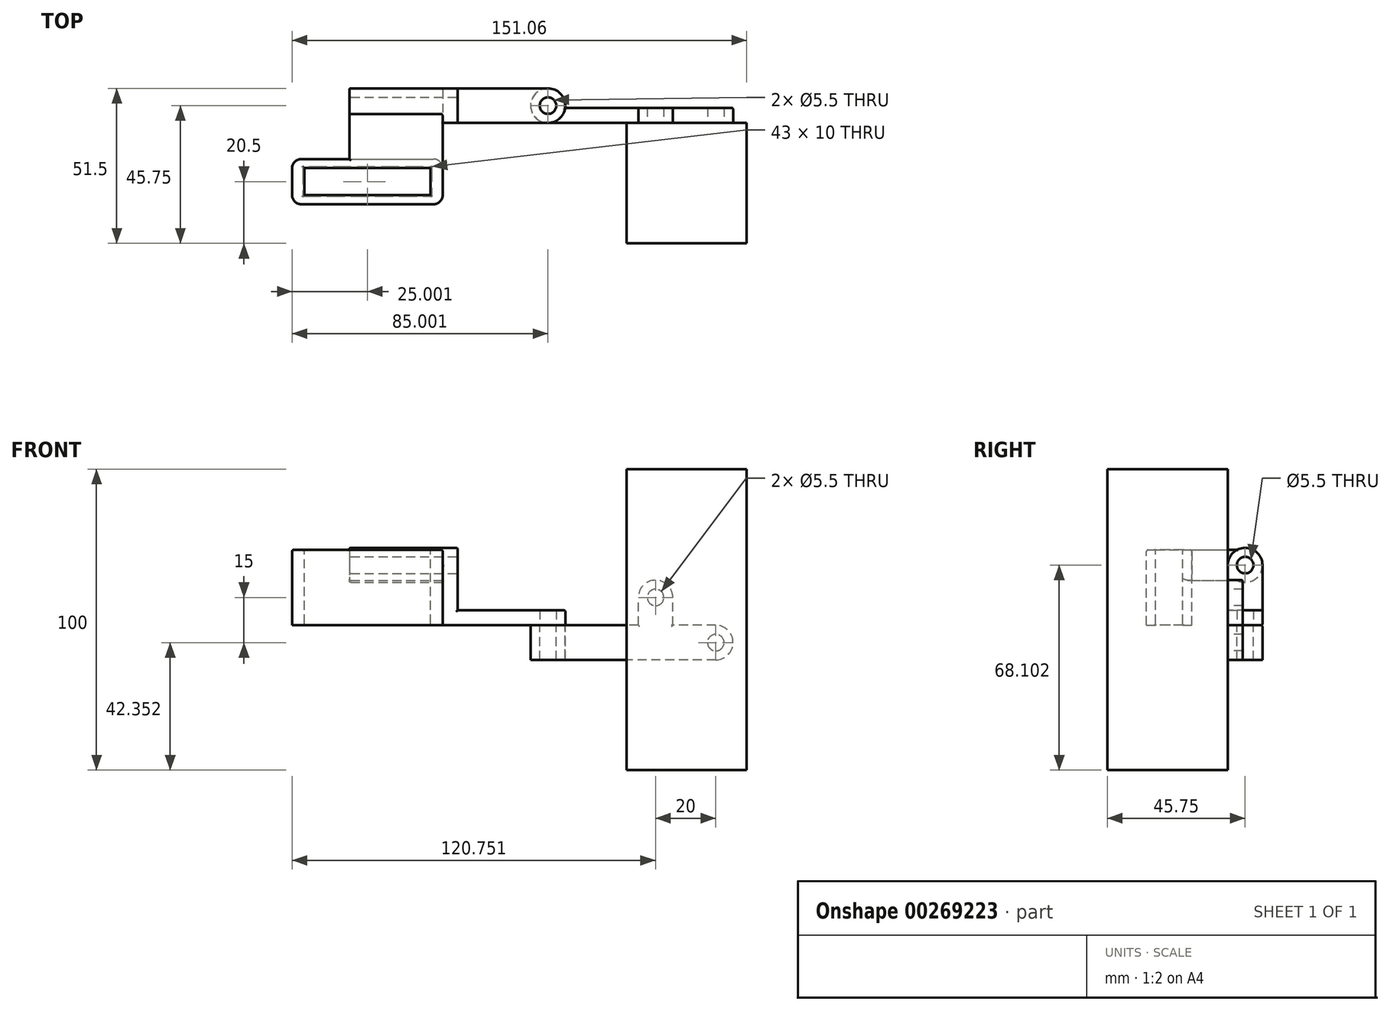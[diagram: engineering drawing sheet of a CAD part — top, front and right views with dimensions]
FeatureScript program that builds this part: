
annotation { "Feature Type Name" : "Feature", "Feature Type Description" : "" }
export const myFeature = defineFeature(function(context is Context, id is Id, definition is map)
    precondition{}
    {
        {
            var Q0;
            Q0=qCreatedBy(makeId("Top.planeOp"),FACE);
            var sketch = newSketch(context, id + "F0", { "sketchPlane" : qUnion([Q0])});
            skLineSegment(sketch, "E0.bottom", {"start": v(-20, 20) * mm, "end": v(20, 20) * mm});
            skLineSegment(sketch, "E0.top", {"start": v(-20, -20) * mm, "end": v(20, -20) * mm});
            skLineSegment(sketch, "E0.left", {"start": v(-20, 20) * mm, "end": v(-20, -20) * mm});
            skLineSegment(sketch, "E0.right", {"start": v(20, 20) * mm, "end": v(20, -20) * mm});
            skPoint(sketch, "E0.middle", {"position": v(0, 0) * mm});
            skSolve(sketch);
        }
        {
            var Q0;
            Q0=makeQuery(id+"F0.imprint","IMPRINT",FACE,{"disambiguationData":[TD([[makeQuery(id+"F0.imprint","IMPRINT",EDGE,{"derivedFrom":sQuery(id+"F0.wireOp",EDGE,"E0.bottom")}),-1.0]])]});
            extrude(context, id + "F1", {"entities" : qUnion([Q0]), "depth" : 100 * mm});
        }
        {
            var Q0;
            Q0=makeQuery(id+"F1.opExtrude","SWEPT_FACE",FACE,{"disambiguationData":[OSD([sQuery(id+"F0.wireOp",EDGE,"E0.bottom")])]});
            var sketch = newSketch(context, id + "F2", { "sketchPlane" : qUnion([Q0])});
            skPoint(sketch, "E1", {"position": v(-9.7, 42.35) * mm});
            skPoint(sketch, "E2", {"position": v(10.3, 57.35) * mm});
            skCircle(sketch, "E3", {"center": v(-9.7, 42.35) * mm, "radius": 5.75 * mm});
            skCircle(sketch, "E4", {"center": v(10.3, 57.35) * mm, "radius": 5.75 * mm});
            skLineSegment(sketch, "E5", {"start": v(-9.7, 48.1) * mm, "end": v(4.56, 48.1) * mm});
            skLineSegment(sketch, "E6", {"start": v(4.56, 48.1) * mm, "end": v(4.56, 57.35) * mm});
            skLineSegment(sketch, "E7", {"start": v(-9.7, 36.6) * mm, "end": v(16.06, 36.6) * mm});
            skLineSegment(sketch, "E8", {"start": v(16.06, 36.6) * mm, "end": v(16.06, 57.35) * mm});
            skLineSegment(sketch, "E9", {"start": v(16.06, 48.1) * mm, "end": v(46.06, 48.1) * mm});
            skLineSegment(sketch, "E10", {"start": v(46.06, 48.1) * mm, "end": v(46.06, 36.6) * mm});
            skLineSegment(sketch, "E11", {"start": v(46.06, 36.6) * mm, "end": v(16.06, 36.6) * mm});
            skSolve(sketch);
        }
        {
            var Q0;
            {var subQ0=sQuery(id+"F2.wireOp",EDGE,"E3");var subQ1=makeQuery(id+"F2.imprint","INTERSECT",VERTEX,{"derivedFrom":[subQ0,sQuery(id+"F2.wireOp",EDGE,"E5")]});Q0=makeQuery(id+"F2.imprint","IMPRINT",FACE,{"disambiguationData":[TD([[makeQuery(id+"F2.imprint","IMPRINT",EDGE,{"disambiguationData":[TD([[subQ1,-1.0]])],"derivedFrom":subQ0}),1.0]])]});}
            var Q1;
            {var subQ0=sQuery(id+"F2.wireOp",EDGE,"E4");var subQ1=makeQuery(id+"F2.imprint","INTERSECT",VERTEX,{"derivedFrom":[subQ0,sQuery(id+"F2.wireOp",EDGE,"E6")]});Q1=makeQuery(id+"F2.imprint","IMPRINT",FACE,{"disambiguationData":[TD([[makeQuery(id+"F2.imprint","IMPRINT",EDGE,{"disambiguationData":[TD([[subQ1,1.0]])],"derivedFrom":subQ0}),1.0]])]});}
            var Q2;
            {var subQ1=sQuery(id+"F2.wireOp",EDGE,"E5");Q2=makeQuery(id+"F2.imprint","IMPRINT",FACE,{"disambiguationData":[TD([[makeQuery(id+"F2.imprint","IMPRINT",EDGE,{"derivedFrom":subQ1}),-1.0]])]});}
            var Q3;
            {var subQ0=sQuery(id+"F2.wireOp",EDGE,"E10");Q3=makeQuery(id+"F2.imprint","IMPRINT",FACE,{"disambiguationData":[TD([[makeQuery(id+"F2.imprint","IMPRINT",EDGE,{"derivedFrom":subQ0}),-1.0]])]});}
            var Q4;
            {var subQ1=sQuery(id+"F2.wireOp",EDGE,"E8");var subQ3=sQuery(id+"F2.wireOp",EDGE,"E9");var subQ4=makeQuery(id+"F2.imprint","INTERSECT",VERTEX,{"derivedFrom":[subQ1,subQ3]});Q4=makeQuery(id+"F2.imprint","IMPRINT",FACE,{"disambiguationData":[TD([[makeQuery(id+"F2.imprint","IMPRINT",EDGE,{"disambiguationData":[TD([[subQ4,1.0]])],"derivedFrom":subQ1}),-1.0]])]});}
            extrude(context, id + "F3", {"entities" : qUnion([Q0, Q1, Q2, Q3, Q4]), "depth" : 5 * mm});
        }
        {
            var Q0;
            Q0=sQuery(id+"F2.wireOp",VERTEX,"E2");
            var Q1;
            Q1=sQuery(id+"F2.wireOp",VERTEX,"E1");
            var Q2;
            Q2=makeQuery(id+"F3.opExtrude","SWEPT_BODY",BODY,{"disambiguationData":[OSD([sQuery(id+"F2.wireOp",EDGE,"E3"),sQuery(id+"F2.wireOp",EDGE,"E4"),sQuery(id+"F2.wireOp",EDGE,"E5"),sQuery(id+"F2.wireOp",EDGE,"E6"),sQuery(id+"F2.wireOp",EDGE,"E7"),sQuery(id+"F2.wireOp",EDGE,"E8"),sQuery(id+"F2.wireOp",EDGE,"E9"),sQuery(id+"F2.wireOp",EDGE,"E10"),sQuery(id+"F2.wireOp",EDGE,"E11")])]});
            hole(context, id + "F4", {"style" : HoleStyle.SIMPLE, "endStyle" : HoleEndStyle.THROUGH, "oppositeDirection" : true, "standardTappedOrClearance" : lookupTablePath({ "standard" : "ISO", "fit" : "Normal", "size" : "M5", "type" : "Clearance" }), "standardBlindInLast" : lookupTablePath({ "fit" : "Standard", "standard" : "ISO", "size" : "M5", "type" : "Clearance" }), "holeDiameter" : 5.5 * mm, "isTappedThrough" : true, "tappedDepth" : 13.2 * mm, "tapClearance" : 3, "startFromSketch" : true, "locations" : qUnion([Q0, Q1]), "scope" : qUnion([Q2])});
        }
        {
            var Q0;
            Q0=makeQuery(id+"F3.opExtrude","SWEPT_FACE",FACE,{"disambiguationData":[OSD([sQuery(id+"F2.wireOp",EDGE,"E9")])]});
            var sketch = newSketch(context, id + "F5", { "sketchPlane" : qUnion([Q0])});
            skPoint(sketch, "E12", {"position": v(-46.06, 25.75) * mm});
            skCircle(sketch, "E13", {"center": v(-46.06, 25.75) * mm, "radius": 5.75 * mm});
            skSolve(sketch);
        }
        {
            var Q0;
            {var subQ1=sQuery(id+"F2.wireOp",EDGE,"E9");var subQ2=makeQuery(id+"F3.opExtrude","SWEPT_EDGE",EDGE,{"disambiguationData":[OSD([subQ1,sQuery(id+"F2.wireOp",EDGE,"E10")])]});Q0=makeQuery(id+"F5.imprint","IMPRINT",FACE,{"disambiguationData":[TD([[makeQuery(id+"F5.imprint","IMPRINT",EDGE,{"derivedFrom":subQ2}),-1.0]])]});}
            var Q1;
            Q1=makeQuery(id+"F3.opExtrude","SWEPT_FACE",FACE,{"disambiguationData":[OSD([sQuery(id+"F2.wireOp",EDGE,"E7"),sQuery(id+"F2.wireOp",EDGE,"E11")])]});
            extrude(context, id + "F6", {"entities" : qUnion([Q0]), "operationType" : NewBodyOperationType.ADD, "endBound" : BoundingType.UP_TO_SURFACE, "oppositeDirection" : true, "endBoundEntityFace" : qUnion([Q1]), "depth" : 25 * mm});
        }
        {
            var Q0;
            Q0=sQuery(id+"F5.wireOp",VERTEX,"E12");
            var Q1;
            Q1=makeQuery(id+"F3.opExtrude","SWEPT_BODY",BODY,{"disambiguationData":[OSD([sQuery(id+"F2.wireOp",EDGE,"E3"),sQuery(id+"F2.wireOp",EDGE,"E4"),sQuery(id+"F2.wireOp",EDGE,"E5"),sQuery(id+"F2.wireOp",EDGE,"E6"),sQuery(id+"F2.wireOp",EDGE,"E7"),sQuery(id+"F2.wireOp",EDGE,"E8"),sQuery(id+"F2.wireOp",EDGE,"E9"),sQuery(id+"F2.wireOp",EDGE,"E10"),sQuery(id+"F2.wireOp",EDGE,"E11")])]});
            hole(context, id + "F7", {"style" : HoleStyle.SIMPLE, "endStyle" : HoleEndStyle.THROUGH, "standardTappedOrClearance" : lookupTablePath({ "standard" : "ISO", "fit" : "Normal", "size" : "M5", "type" : "Clearance" }), "standardBlindInLast" : lookupTablePath({ "fit" : "Standard", "standard" : "ISO", "size" : "M5", "type" : "Clearance" }), "holeDiameter" : 5.5 * mm, "isTappedThrough" : true, "tappedDepth" : 13.2 * mm, "tapClearance" : 3, "startFromSketch" : true, "locations" : qUnion([Q0]), "scope" : qUnion([Q1])});
        }
        {
            var Q0;
            {var subQ1=sQuery(id+"F2.wireOp",EDGE,"E9");var subQ2=makeQuery(id+"F3.opExtrude","CAP_EDGE",EDGE,{"disambiguationData":[OSD([subQ1])],"isStart":true});Q0=makeQuery(id+"F5.imprint","IMPRINT",FACE,{"disambiguationData":[TD([[makeQuery(id+"F5.imprint","IMPRINT",EDGE,{"derivedFrom":subQ2}),-1.0]])]});}
            var sketch = newSketch(context, id + "F8", { "sketchPlane" : qUnion([Q0])});
            skPoint(sketch, "E14", {"position": v(-46.06, 25.75) * mm});
            skCircle(sketch, "E15", {"center": v(-46.06, 25.75) * mm, "radius": 5.75 * mm});
            skLineSegment(sketch, "E16", {"start": v(-46.06, 31.5) * mm, "end": v(-76.06, 31.5) * mm});
            skLineSegment(sketch, "E17", {"start": v(-76.06, 31.5) * mm, "end": v(-76.06, 20) * mm});
            skLineSegment(sketch, "E18", {"start": v(-76.06, 20) * mm, "end": v(-46.06, 20) * mm});
            skSolve(sketch);
        }
        {
            var Q0;
            {var subQ2=sQuery(id+"F8.wireOp",EDGE,"E16");Q0=makeQuery(id+"F8.imprint","IMPRINT",FACE,{"disambiguationData":[TD([[makeQuery(id+"F8.imprint","IMPRINT",EDGE,{"derivedFrom":subQ2}),1.0]])]});}
            var Q1;
            {var subQ0=sQuery(id+"F8.wireOp",EDGE,"E15");var subQ3=makeQuery(id+"F8.imprint","INTERSECT",VERTEX,{"derivedFrom":[subQ0,sQuery(id+"F8.wireOp",EDGE,"E16")]});Q1=makeQuery(id+"F8.imprint","IMPRINT",FACE,{"disambiguationData":[TD([[makeQuery(id+"F8.imprint","IMPRINT",EDGE,{"disambiguationData":[TD([[subQ3,-1.0]])],"derivedFrom":subQ0}),1.0]])]});}
            extrude(context, id + "F9", {"entities" : qUnion([Q0, Q1]), "depth" : 5 * mm});
        }
        {
            var Q0;
            Q0=sQuery(id+"F5.wireOp",VERTEX,"E12");
            var Q1;
            Q1=makeQuery(id+"F9.opExtrude","SWEPT_BODY",BODY,{"disambiguationData":[OSD([sQuery(id+"F8.wireOp",EDGE,"E15"),sQuery(id+"F8.wireOp",EDGE,"E16"),sQuery(id+"F8.wireOp",EDGE,"E17"),sQuery(id+"F8.wireOp",EDGE,"E18")])]});
            hole(context, id + "F10", {"style" : HoleStyle.SIMPLE, "endStyle" : HoleEndStyle.THROUGH, "oppositeDirection" : true, "standardTappedOrClearance" : lookupTablePath({ "standard" : "ISO", "fit" : "Normal", "size" : "M5", "type" : "Clearance" }), "standardBlindInLast" : lookupTablePath({ "fit" : "Standard", "standard" : "ISO", "size" : "M5", "type" : "Clearance" }), "holeDiameter" : 5.5 * mm, "isTappedThrough" : true, "tappedDepth" : 13.2 * mm, "tapClearance" : 3, "startFromSketch" : true, "locations" : qUnion([Q0]), "scope" : qUnion([Q1])});
        }
        {
            var Q0;
            Q0=makeQuery(id+"F9.opExtrude","SWEPT_FACE",FACE,{"disambiguationData":[OSD([sQuery(id+"F8.wireOp",EDGE,"E17")])]});
            var sketch = newSketch(context, id + "F11", { "sketchPlane" : qUnion([Q0])});
            skLineSegment(sketch, "E19.bottom", {"start": v(-31.5, 48.1) * mm, "end": v(-20, 48.1) * mm});
            skLineSegment(sketch, "E19.top", {"start": v(-31.5, 68.1) * mm, "end": v(-20, 68.1) * mm});
            skLineSegment(sketch, "E19.left", {"start": v(-31.5, 48.1) * mm, "end": v(-31.5, 68.1) * mm});
            skLineSegment(sketch, "E19.right", {"start": v(-20, 48.1) * mm, "end": v(-20, 68.1) * mm});
            skCircle(sketch, "E20", {"center": v(-25.75, 68.1) * mm, "radius": 5.75 * mm});
            skSolve(sketch);
        }
        {
            var Q0;
            {var subQ0=sQuery(id+"F11.wireOp",EDGE,"E19.top");Q0=makeQuery(id+"F11.imprint","IMPRINT",FACE,{"disambiguationData":[TD([[makeQuery(id+"F11.imprint","IMPRINT",EDGE,{"derivedFrom":subQ0}),-1.0]])]});}
            var Q1;
            {var subQ0=sQuery(id+"F11.wireOp",EDGE,"E19.top");Q1=makeQuery(id+"F11.imprint","IMPRINT",FACE,{"disambiguationData":[TD([[makeQuery(id+"F11.imprint","IMPRINT",EDGE,{"derivedFrom":subQ0}),1.0]])]});}
            var Q2;
            {var subQ1=makeQuery(id+"F9.opExtrude","CAP_EDGE",EDGE,{"disambiguationData":[OSD([sQuery(id+"F8.wireOp",EDGE,"E17")])],"isStart":false});Q2=makeQuery(id+"F11.imprint","IMPRINT",FACE,{"disambiguationData":[TD([[makeQuery(id+"F11.imprint","IMPRINT",EDGE,{"derivedFrom":subQ1}),1.0]])]});}
            var Q3;
            {var subQ0=sQuery(id+"F11.wireOp",EDGE,"E19.bottom");Q3=makeQuery(id+"F11.imprint","IMPRINT",FACE,{"disambiguationData":[TD([[makeQuery(id+"F11.imprint","IMPRINT",EDGE,{"derivedFrom":subQ0}),1.0]])]});}
            extrude(context, id + "F12", {"entities" : qUnion([Q0, Q1, Q2, Q3]), "operationType" : NewBodyOperationType.ADD, "depth" : 5 * mm});
        }
        {
            var Q0;
            Q0=sQuery(id+"F11.wireOp",VERTEX,"E20.center");
            var Q1;
            Q1=makeQuery(id+"F9.opExtrude","SWEPT_BODY",BODY,{"disambiguationData":[OSD([sQuery(id+"F8.wireOp",EDGE,"E15"),sQuery(id+"F8.wireOp",EDGE,"E16"),sQuery(id+"F8.wireOp",EDGE,"E17"),sQuery(id+"F8.wireOp",EDGE,"E18")])]});
            hole(context, id + "F13", {"style" : HoleStyle.SIMPLE, "endStyle" : HoleEndStyle.THROUGH, "oppositeDirection" : true, "standardTappedOrClearance" : lookupTablePath({ "standard" : "ISO", "fit" : "Normal", "size" : "M5", "type" : "Clearance" }), "standardBlindInLast" : lookupTablePath({ "fit" : "Standard", "standard" : "ISO", "size" : "M5", "type" : "Clearance" }), "holeDiameter" : 5.5 * mm, "isTappedThrough" : true, "tappedDepth" : 13.2 * mm, "tapClearance" : 3, "startFromSketch" : true, "locations" : qUnion([Q0]), "scope" : qUnion([Q1])});
        }
        {
            var Q0;
            Q0=makeQuery(id+"F12.opExtrude","CAP_FACE",FACE,{"disambiguationData":[OSD([sQuery(id+"F11.wireOp",EDGE,"E19.bottom"),sQuery(id+"F11.wireOp",EDGE,"E19.left"),sQuery(id+"F11.wireOp",EDGE,"E19.right"),sQuery(id+"F11.wireOp",EDGE,"E20")])],"isStart":false});
            var sketch = newSketch(context, id + "F14", { "sketchPlane" : qUnion([Q0])});
            skCircle(sketch, "E21", {"center": v(-25.75, 68.1) * mm, "radius": 5.75 * mm});
            skSolve(sketch);
        }
        {
            var Q0;
            {var subQ0=sQuery(id+"F14.wireOp",EDGE,"E21");var subQ1=sQuery(id+"F11.wireOp",EDGE,"E19.left");var subQ2=makeQuery(id+"F14.imprint","INTERSECT",VERTEX,{"derivedFrom":[makeQuery(id+"F12.opExtrude","CAP_EDGE",EDGE,{"disambiguationData":[OSD([subQ1])],"isStart":false}),subQ0]});Q0=makeQuery(id+"F14.imprint","IMPRINT",FACE,{"disambiguationData":[TD([[makeQuery(id+"F14.imprint","IMPRINT",EDGE,{"disambiguationData":[TD([[subQ2,1.0]])],"derivedFrom":subQ0}),1.0]])]});}
            extrude(context, id + "F15", {"entities" : qUnion([Q0]), "depth" : 31 * mm});
        }
        {
            var Q0;
            Q0=makeQuery(id+"F15.opExtrude","CAP_FACE",FACE,{"disambiguationData":[OSD([sQuery(id+"F11.wireOp",EDGE,"E19.bottom"),sQuery(id+"F11.wireOp",EDGE,"E19.left"),sQuery(id+"F11.wireOp",EDGE,"E19.right"),sQuery(id+"F11.wireOp",EDGE,"E20"),sQuery(id+"F13.hole-0.sketch.wireOp",EDGE,"core_line_2"),sQuery(id+"F14.wireOp",EDGE,"E21")])],"isStart":true});
            var sketch = newSketch(context, id + "F16", { "sketchPlane" : qUnion([Q0])});
            skLineSegment(sketch, "E22.bottom", {"start": v(8, 73.15) * mm, "end": v(23, 73.15) * mm});
            skLineSegment(sketch, "E22.top", {"start": v(8, 63.05) * mm, "end": v(23, 63.05) * mm});
            skLineSegment(sketch, "E22.left", {"start": v(8, 73.15) * mm, "end": v(8, 63.05) * mm});
            skLineSegment(sketch, "E22.right", {"start": v(23, 73.15) * mm, "end": v(23, 63.05) * mm});
            skSolve(sketch);
        }
        {
            var Q0;
            {var subQ0=sQuery(id+"F16.wireOp",EDGE,"E22.bottom");Q0=makeQuery(id+"F16.imprint","IMPRINT",FACE,{"disambiguationData":[TD([[makeQuery(id+"F16.imprint","IMPRINT",EDGE,{"derivedFrom":subQ0}),-1.0]])]});}
            extrude(context, id + "F17", {"entities" : qUnion([Q0]), "operationType" : NewBodyOperationType.ADD, "oppositeDirection" : true, "depth" : 31 * mm});
        }
        {
            var Q0;
            Q0=makeQuery(id+"F17.opExtrude","SWEPT_FACE",FACE,{"disambiguationData":[OSD([sQuery(id+"F16.wireOp",EDGE,"E22.bottom")])]});
            var sketch = newSketch(context, id + "F18", { "sketchPlane" : qUnion([Q0])});
            skLineSegment(sketch, "E23.bottom", {"start": v(-81.06, 8) * mm, "end": v(-131.06, 8) * mm});
            skLineSegment(sketch, "E23.top", {"start": v(-81.06, -7) * mm, "end": v(-131.06, -7) * mm});
            skLineSegment(sketch, "E23.left", {"start": v(-81.06, 8) * mm, "end": v(-81.06, -7) * mm});
            skLineSegment(sketch, "E23.right", {"start": v(-131.06, 8) * mm, "end": v(-131.06, -7) * mm});
            skLineSegment(sketch, "E24.bottom", {"start": v(-127.06, 5) * mm, "end": v(-85.06, 5) * mm});
            skLineSegment(sketch, "E24.top", {"start": v(-127.06, -4) * mm, "end": v(-85.06, -4) * mm});
            skLineSegment(sketch, "E24.left", {"start": v(-127.06, 5) * mm, "end": v(-127.06, -4) * mm});
            skLineSegment(sketch, "E24.right", {"start": v(-85.06, 5) * mm, "end": v(-85.06, -4) * mm});
            skPoint(sketch, "E25", {"position": v(-106.06, 5) * mm});
            skPoint(sketch, "E26", {"position": v(-85.06, 0.5) * mm});
            skPoint(sketch, "E27", {"position": v(-81.06, 0.5) * mm});
            skPoint(sketch, "E28", {"position": v(-106.06, 8) * mm});
            skSolve(sketch);
        }
        {
            var Q0;
            Q0=makeQuery(id+"F18.imprint","IMPRINT",FACE,{"disambiguationData":[TD([[makeQuery(id+"F18.imprint","IMPRINT",EDGE,{"derivedFrom":sQuery(id+"F18.wireOp",EDGE,"E23.top")}),-1.0]])]});
            extrude(context, id + "F19", {"entities" : qUnion([Q0]), "operationType" : NewBodyOperationType.ADD, "oppositeDirection" : true, "depth" : 25 * mm});
        }
        {
            var Q0;
            Q0=makeQuery(id+"F19.opExtrude","SWEPT_EDGE",EDGE,{"disambiguationData":[OSD([sQuery(id+"F18.wireOp",EDGE,"E23.bottom"),sQuery(id+"F18.wireOp",EDGE,"E23.right")])]});
            var Q1;
            Q1=makeQuery(id+"F19.opExtrude","SWEPT_EDGE",EDGE,{"disambiguationData":[OSD([sQuery(id+"F18.wireOp",EDGE,"E23.top"),sQuery(id+"F18.wireOp",EDGE,"E23.right")])]});
            var Q2;
            Q2=makeQuery(id+"F19.opExtrude","SWEPT_EDGE",EDGE,{"disambiguationData":[OSD([sQuery(id+"F18.wireOp",EDGE,"E23.top"),sQuery(id+"F18.wireOp",EDGE,"E23.left")])]});
            var Q3;
            Q3=makeQuery(id+"F19.opExtrude","SWEPT_EDGE",EDGE,{"disambiguationData":[OSD([sQuery(id+"F16.wireOp",EDGE,"E22.bottom"),sQuery(id+"F18.wireOp",EDGE,"E23.bottom"),sQuery(id+"F18.wireOp",EDGE,"E23.left")])]});
            fillet(context, id + "F20", {"entities" : qUnion([Q0, Q1, Q2, Q3]), "radius" : 3 * mm, "tangentPropagation" : true, "allowEdgeOverflow" : false});
        }
        {
            var Q0;
            Q0=makeQuery(id+"F17.opExtrude","CAP_EDGE",EDGE,{"disambiguationData":[OSD([sQuery(id+"F16.wireOp",EDGE,"E22.top")])],"isStart":true});
            var Q1;
            Q1=makeQuery(id+"F19.boolean.opBoolean","MERGE",EDGE,{"derivedFrom":[makeQuery(id+"F17.opExtrude","CAP_EDGE",EDGE,{"disambiguationData":[OSD([sQuery(id+"F16.wireOp",EDGE,"E22.bottom")])],"isStart":true}),makeQuery(id+"F19.opExtrude","CAP_EDGE",EDGE,{"disambiguationData":[OSD([sQuery(id+"F18.wireOp",EDGE,"E23.left")])],"isStart":true})]});
            var Q2;
            Q2=makeQuery(id+"F15.opExtrude","CAP_EDGE",EDGE,{"disambiguationData":[OSD([sQuery(id+"F14.wireOp",EDGE,"E21")])],"isStart":true});
            var Q3;
            Q3=makeQuery(id+"F15.opExtrude","CAP_EDGE",EDGE,{"disambiguationData":[OSD([sQuery(id+"F11.wireOp",EDGE,"E19.bottom"),sQuery(id+"F11.wireOp",EDGE,"E19.left"),sQuery(id+"F11.wireOp",EDGE,"E19.right"),sQuery(id+"F11.wireOp",EDGE,"E20"),sQuery(id+"F13.hole-0.sketch.wireOp",EDGE,"core_line_2")])],"isStart":true});
            var Q4;
            Q4=makeQuery(id+"F19.opExtrude","CAP_EDGE",EDGE,{"disambiguationData":[OSD([sQuery(id+"F18.wireOp",EDGE,"E24.top")])],"isStart":true});
            var Q5;
            Q5=makeQuery(id+"F19.opExtrude","CAP_EDGE",EDGE,{"disambiguationData":[OSD([sQuery(id+"F18.wireOp",EDGE,"E24.right")])],"isStart":true});
            var Q6;
            Q6=makeQuery(id+"F19.opExtrude","CAP_EDGE",EDGE,{"disambiguationData":[OSD([sQuery(id+"F18.wireOp",EDGE,"E24.bottom")])],"isStart":true});
            var Q7;
            Q7=makeQuery(id+"F19.opExtrude","CAP_EDGE",EDGE,{"disambiguationData":[OSD([sQuery(id+"F18.wireOp",EDGE,"E24.left")])],"isStart":true});
            var Q8;
            Q8=makeQuery(id+"F17.opExtrude","CAP_EDGE",EDGE,{"disambiguationData":[OSD([sQuery(id+"F16.wireOp",EDGE,"E22.bottom")])],"isStart":false});
            var Q9;
            Q9=makeQuery(id+"F15.opExtrude","CAP_EDGE",EDGE,{"disambiguationData":[OSD([sQuery(id+"F14.wireOp",EDGE,"E21")])],"isStart":false});
            var Q10;
            Q10=makeQuery(id+"F17.opExtrude","CAP_EDGE",EDGE,{"disambiguationData":[OSD([sQuery(id+"F16.wireOp",EDGE,"E22.top")])],"isStart":false});
            var Q11;
            Q11=makeQuery(id+"F15.opExtrude","CAP_EDGE",EDGE,{"disambiguationData":[OSD([sQuery(id+"F11.wireOp",EDGE,"E19.bottom"),sQuery(id+"F11.wireOp",EDGE,"E19.left"),sQuery(id+"F11.wireOp",EDGE,"E19.right"),sQuery(id+"F11.wireOp",EDGE,"E20"),sQuery(id+"F13.hole-0.sketch.wireOp",EDGE,"core_line_2")])],"isStart":false});
            var Q12;
            Q12=makeQuery(id+"F17.opExtrude","CAP_EDGE",EDGE,{"disambiguationData":[OSD([sQuery(id+"F16.wireOp",EDGE,"E22.left")])],"isStart":false});
            var Q13;
            Q13=makeQuery(id+"F17.opExtrude","SWEPT_EDGE",EDGE,{"disambiguationData":[OSD([sQuery(id+"F16.wireOp",EDGE,"E22.top"),sQuery(id+"F16.wireOp",EDGE,"E22.left")])]});
            var Q14;
            Q14=makeQuery(id+"F19.opExtrude","CAP_EDGE",EDGE,{"disambiguationData":[OSD([sQuery(id+"F18.wireOp",EDGE,"E24.bottom")])],"isStart":false});
            var Q15;
            Q15=makeQuery(id+"F19.opExtrude","CAP_EDGE",EDGE,{"disambiguationData":[OSD([sQuery(id+"F18.wireOp",EDGE,"E24.left")])],"isStart":false});
            var Q16;
            Q16=makeQuery(id+"F19.opExtrude","CAP_EDGE",EDGE,{"disambiguationData":[OSD([sQuery(id+"F18.wireOp",EDGE,"E24.top")])],"isStart":false});
            var Q17;
            Q17=makeQuery(id+"F19.opExtrude","CAP_EDGE",EDGE,{"disambiguationData":[OSD([sQuery(id+"F18.wireOp",EDGE,"E24.right")])],"isStart":false});
            var Q18;
            Q18=makeQuery(id+"F13.hole-0.boolean.opBoolean","INTERSECT",EDGE,{"derivedFrom":[makeQuery(id+"F12.opExtrude","CAP_FACE",FACE,{"disambiguationData":[OSD([sQuery(id+"F11.wireOp",EDGE,"E19.bottom"),sQuery(id+"F11.wireOp",EDGE,"E19.left"),sQuery(id+"F11.wireOp",EDGE,"E19.right"),sQuery(id+"F11.wireOp",EDGE,"E20")])],"isStart":false}),makeQuery(id+"F13.hole-0.opRevolve","SWEPT_FACE",FACE,{"disambiguationData":[OSD([sQuery(id+"F13.hole-0.sketch.wireOp",EDGE,"core_line_2")])]})]});
            var Q19;
            Q19=makeQuery(id+"F13.hole-0.boolean.opBoolean","COPY",EDGE,{"derivedFrom":makeQuery(id+"F13.hole-0.opRevolve","SWEPT_EDGE",EDGE,{"disambiguationData":[OSD([sQuery(id+"F13.hole-0.sketch.wireOp",EDGE,"core_line_2"),sQuery(id+"F13.hole-0.sketch.wireOp",EDGE,"core_line_3")])]})});
            var Q20;
            Q20=makeQuery(id+"F7.hole-0.boolean.opBoolean","COPY",EDGE,{"derivedFrom":makeQuery(id+"F7.hole-0.opRevolve","SWEPT_EDGE",EDGE,{"disambiguationData":[OSD([sQuery(id+"F7.hole-0.sketch.wireOp",EDGE,"core_line_2"),sQuery(id+"F7.hole-0.sketch.wireOp",EDGE,"core_line_3")])]})});
            var Q21;
            Q21=makeQuery(id+"F10.hole-0.boolean.opBoolean","INTERSECT",EDGE,{"derivedFrom":[makeQuery(id+"F9.opExtrude","CAP_FACE",FACE,{"disambiguationData":[OSD([sQuery(id+"F8.wireOp",EDGE,"E15"),sQuery(id+"F8.wireOp",EDGE,"E16"),sQuery(id+"F8.wireOp",EDGE,"E17"),sQuery(id+"F8.wireOp",EDGE,"E18")])],"isStart":false}),makeQuery(id+"F10.hole-0.opRevolve","SWEPT_FACE",FACE,{"disambiguationData":[OSD([sQuery(id+"F10.hole-0.sketch.wireOp",EDGE,"core_line_2")])]})]});
            var Q22;
            Q22=makeQuery(id+"F9.opExtrude","CAP_EDGE",EDGE,{"disambiguationData":[OSD([sQuery(id+"F8.wireOp",EDGE,"E16")])],"isStart":false});
            var Q23;
            Q23=makeQuery(id+"F12.opExtrude","CAP_EDGE",EDGE,{"disambiguationData":[OSD([sQuery(id+"F11.wireOp",EDGE,"E19.left")])],"isStart":true});
            var Q24;
            Q24=makeQuery(id+"F12.boolean.opBoolean","MERGE",EDGE,{"derivedFrom":[makeQuery(id+"F9.opExtrude","CAP_EDGE",EDGE,{"disambiguationData":[OSD([sQuery(id+"F8.wireOp",EDGE,"E18")])],"isStart":true}),makeQuery(id+"F12.opExtrude","SWEPT_EDGE",EDGE,{"disambiguationData":[OSD([sQuery(id+"F11.wireOp",EDGE,"E19.bottom"),sQuery(id+"F11.wireOp",EDGE,"E19.right")])]})]});
            var Q25;
            Q25=makeQuery(id+"F12.opExtrude","CAP_EDGE",EDGE,{"disambiguationData":[OSD([sQuery(id+"F11.wireOp",EDGE,"E19.bottom")])],"isStart":false});
            var Q26;
            Q26=makeQuery(id+"F12.opExtrude","CAP_EDGE",EDGE,{"disambiguationData":[OSD([sQuery(id+"F11.wireOp",EDGE,"E19.left")])],"isStart":false});
            var Q27;
            {var subQ0=sQuery(id+"F2.wireOp",EDGE,"E11");var subQ1=sQuery(id+"F2.wireOp",EDGE,"E7");Q27=makeQuery(id+"F7.hole-0.boolean.opBoolean","INTERSECT",EDGE,{"derivedFrom":[makeQuery(id+"F6.boolean.opBoolean","MERGE",FACE,{"derivedFrom":[makeQuery(id+"F3.opExtrude","SWEPT_FACE",FACE,{"disambiguationData":[OSD([subQ1,subQ0])]}),makeQuery(id+"F6.opExtrude","CAP_FACE",FACE,{"disambiguationData":[OSD([subQ1,subQ0])],"isStart":false})]}),makeQuery(id+"F7.hole-0.opRevolve","SWEPT_FACE",FACE,{"disambiguationData":[OSD([sQuery(id+"F7.hole-0.sketch.wireOp",EDGE,"core_line_2")])]})]});}
            var Q28;
            {var subQ0=sQuery(id+"F5.wireOp",EDGE,"E13");var subQ1=sQuery(id+"F2.wireOp",EDGE,"E9");Q28=makeQuery(id+"F6.opExtrude","TWEAK_EDGE",EDGE,{"derivedFrom":[makeQuery(id+"F3.opExtrude","SWEPT_FACE",FACE,{"disambiguationData":[OSD([sQuery(id+"F2.wireOp",EDGE,"E7"),sQuery(id+"F2.wireOp",EDGE,"E11")])]}),makeQuery(id+"F5.imprint","IMPRINT",EDGE,{"disambiguationData":[TD([[makeQuery(id+"F5.imprint","INTERSECT",VERTEX,{"derivedFrom":[makeQuery(id+"F3.opExtrude","CAP_EDGE",EDGE,{"disambiguationData":[OSD([subQ1])],"isStart":false}),subQ0]}),-1.0]])],"derivedFrom":subQ0})]});}
            var Q29;
            Q29=makeQuery(id+"F3.opExtrude","CAP_EDGE",EDGE,{"disambiguationData":[OSD([sQuery(id+"F2.wireOp",EDGE,"E7"),sQuery(id+"F2.wireOp",EDGE,"E11")])],"isStart":false});
            var Q30;
            Q30=makeQuery(id+"F3.opExtrude","CAP_EDGE",EDGE,{"disambiguationData":[OSD([sQuery(id+"F2.wireOp",EDGE,"E9")])],"isStart":false});
            var Q31;
            Q31=makeQuery(id+"F6.opExtrude","CAP_EDGE",EDGE,{"disambiguationData":[OSD([sQuery(id+"F5.wireOp",EDGE,"E13")])],"isStart":true});
            var Q32;
            Q32=makeQuery(id+"F3.opExtrude","CAP_EDGE",EDGE,{"disambiguationData":[OSD([sQuery(id+"F2.wireOp",EDGE,"E8")])],"isStart":false});
            var Q33;
            Q33=makeQuery(id+"F3.opExtrude","CAP_EDGE",EDGE,{"disambiguationData":[OSD([sQuery(id+"F2.wireOp",EDGE,"E8")])],"isStart":true});
            var Q34;
            Q34=makeQuery(id+"F4.hole-0.boolean.opBoolean","COPY",EDGE,{"derivedFrom":makeQuery(id+"F4.hole-0.opRevolve","SWEPT_EDGE",EDGE,{"disambiguationData":[OSD([sQuery(id+"F4.hole-0.sketch.wireOp",EDGE,"core_line_2"),sQuery(id+"F4.hole-0.sketch.wireOp",EDGE,"core_line_3")])]})});
            var Q35;
            Q35=makeQuery(id+"F4.hole-0.boolean.opBoolean","INTERSECT",EDGE,{"derivedFrom":[makeQuery(id+"F3.opExtrude","CAP_FACE",FACE,{"disambiguationData":[OSD([sQuery(id+"F2.wireOp",EDGE,"E3"),sQuery(id+"F2.wireOp",EDGE,"E4"),sQuery(id+"F2.wireOp",EDGE,"E5"),sQuery(id+"F2.wireOp",EDGE,"E6"),sQuery(id+"F2.wireOp",EDGE,"E7"),sQuery(id+"F2.wireOp",EDGE,"E8"),sQuery(id+"F2.wireOp",EDGE,"E9"),sQuery(id+"F2.wireOp",EDGE,"E10"),sQuery(id+"F2.wireOp",EDGE,"E11")])],"isStart":false}),makeQuery(id+"F4.hole-0.opRevolve","SWEPT_FACE",FACE,{"disambiguationData":[OSD([sQuery(id+"F4.hole-0.sketch.wireOp",EDGE,"core_line_2")])]})]});
            var Q36;
            Q36=makeQuery(id+"F4.hole-1.boolean.opBoolean","COPY",EDGE,{"derivedFrom":makeQuery(id+"F4.hole-1.opRevolve","SWEPT_EDGE",EDGE,{"disambiguationData":[OSD([sQuery(id+"F4.hole-1.sketch.wireOp",EDGE,"core_line_2"),sQuery(id+"F4.hole-1.sketch.wireOp",EDGE,"core_line_3")])]})});
            var Q37;
            Q37=makeQuery(id+"F4.hole-1.boolean.opBoolean","INTERSECT",EDGE,{"derivedFrom":[makeQuery(id+"F3.opExtrude","CAP_FACE",FACE,{"disambiguationData":[OSD([sQuery(id+"F2.wireOp",EDGE,"E3"),sQuery(id+"F2.wireOp",EDGE,"E4"),sQuery(id+"F2.wireOp",EDGE,"E5"),sQuery(id+"F2.wireOp",EDGE,"E6"),sQuery(id+"F2.wireOp",EDGE,"E7"),sQuery(id+"F2.wireOp",EDGE,"E8"),sQuery(id+"F2.wireOp",EDGE,"E9"),sQuery(id+"F2.wireOp",EDGE,"E10"),sQuery(id+"F2.wireOp",EDGE,"E11")])],"isStart":false}),makeQuery(id+"F4.hole-1.opRevolve","SWEPT_FACE",FACE,{"disambiguationData":[OSD([sQuery(id+"F4.hole-1.sketch.wireOp",EDGE,"core_line_2")])]})]});
            fillet(context, id + "F21", {"entities" : qUnion([Q0, Q1, Q2, Q3, Q4, Q5, Q6, Q7, Q8, Q9, Q10, Q11, Q12, Q13, Q14, Q15, Q16, Q17, Q18, Q19, Q20, Q21, Q22, Q23, Q24, Q25, Q26, Q27, Q28, Q29, Q30, Q31, Q32, Q33, Q34, Q35, Q36, Q37]), "radius" : 0.5 * mm, "tangentPropagation" : true, "allowEdgeOverflow" : false});
        }
    });
